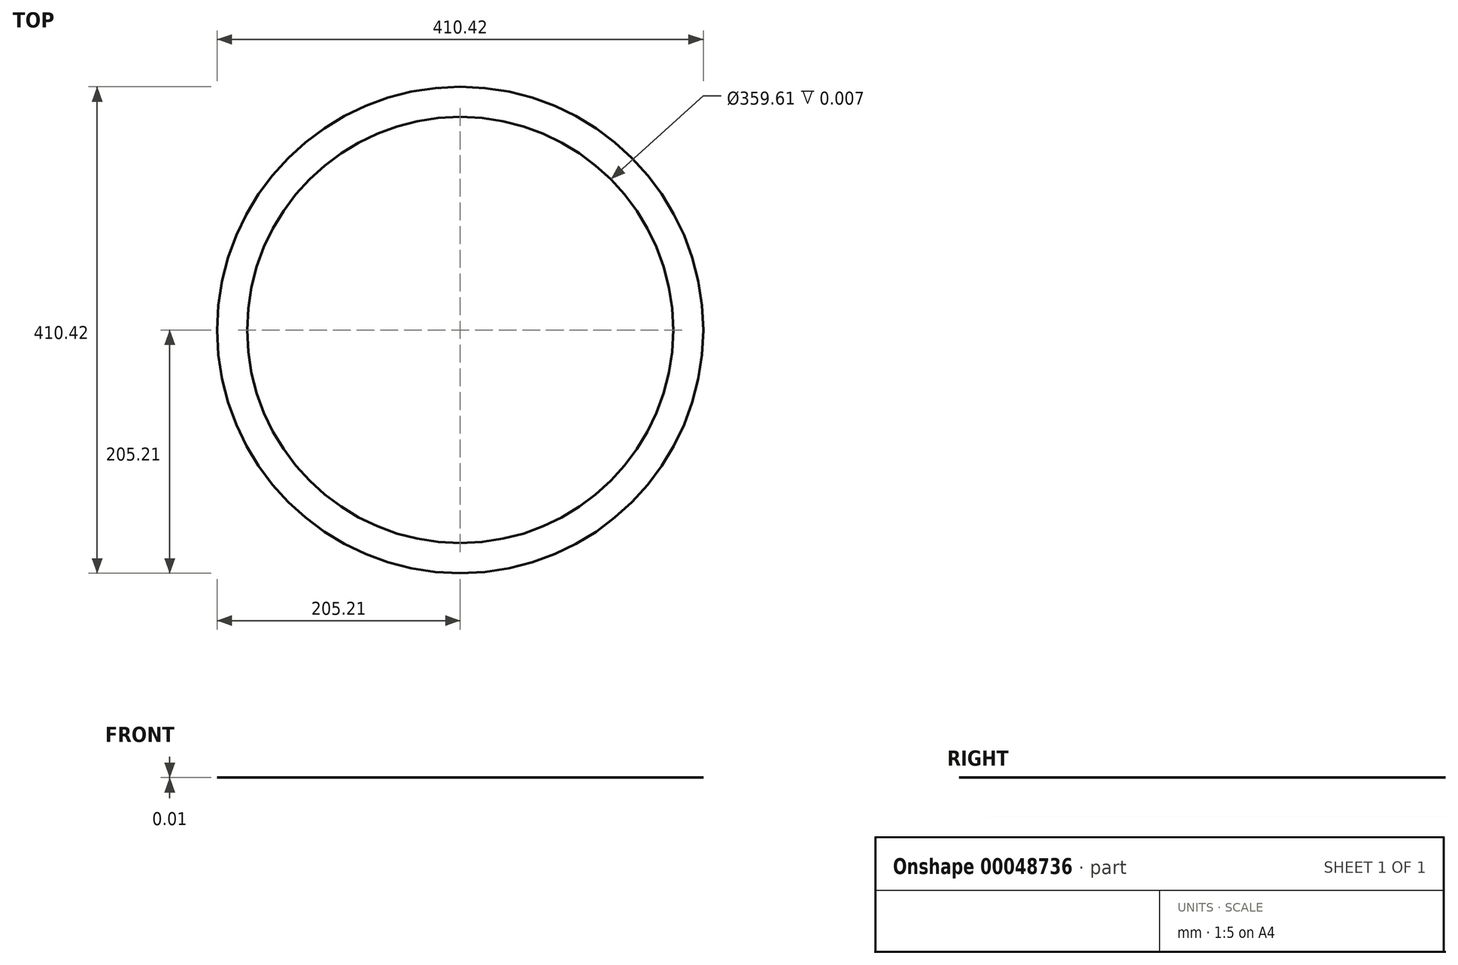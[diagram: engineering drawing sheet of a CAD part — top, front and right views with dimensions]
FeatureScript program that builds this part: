
annotation { "Feature Type Name" : "Feature", "Feature Type Description" : "" }
export const myFeature = defineFeature(function(context is Context, id is Id, definition is map)
    precondition{}
    {
        {
            var Q0;
            Q0=qCreatedBy(makeId("Top.planeOp"),FACE);
            var sketch = newSketch(context, id + "F0", { "sketchPlane" : qUnion([Q0])});
            skCircle(sketch, "E0", {"center": v(0, 0) * mm, "radius": 205.2 * mm});
            skCircle(sketch, "E1", {"center": v(0, 0) * mm, "radius": 179.8 * mm});
            skSolve(sketch);
        }
        {
            var Q0;
            Q0=makeQuery(id+"F0.imprint","IMPRINT",FACE,{"disambiguationData":[TD([[makeQuery(id+"F0.imprint","IMPRINT",EDGE,{"derivedFrom":sQuery(id+"F0.wireOp",EDGE,"E0")}),1.0]])]});
            extrude(context, id + "F1", {"entities" : qUnion([Q0]), "depth" : 3 / 406.4 * mm});
        }
    });
